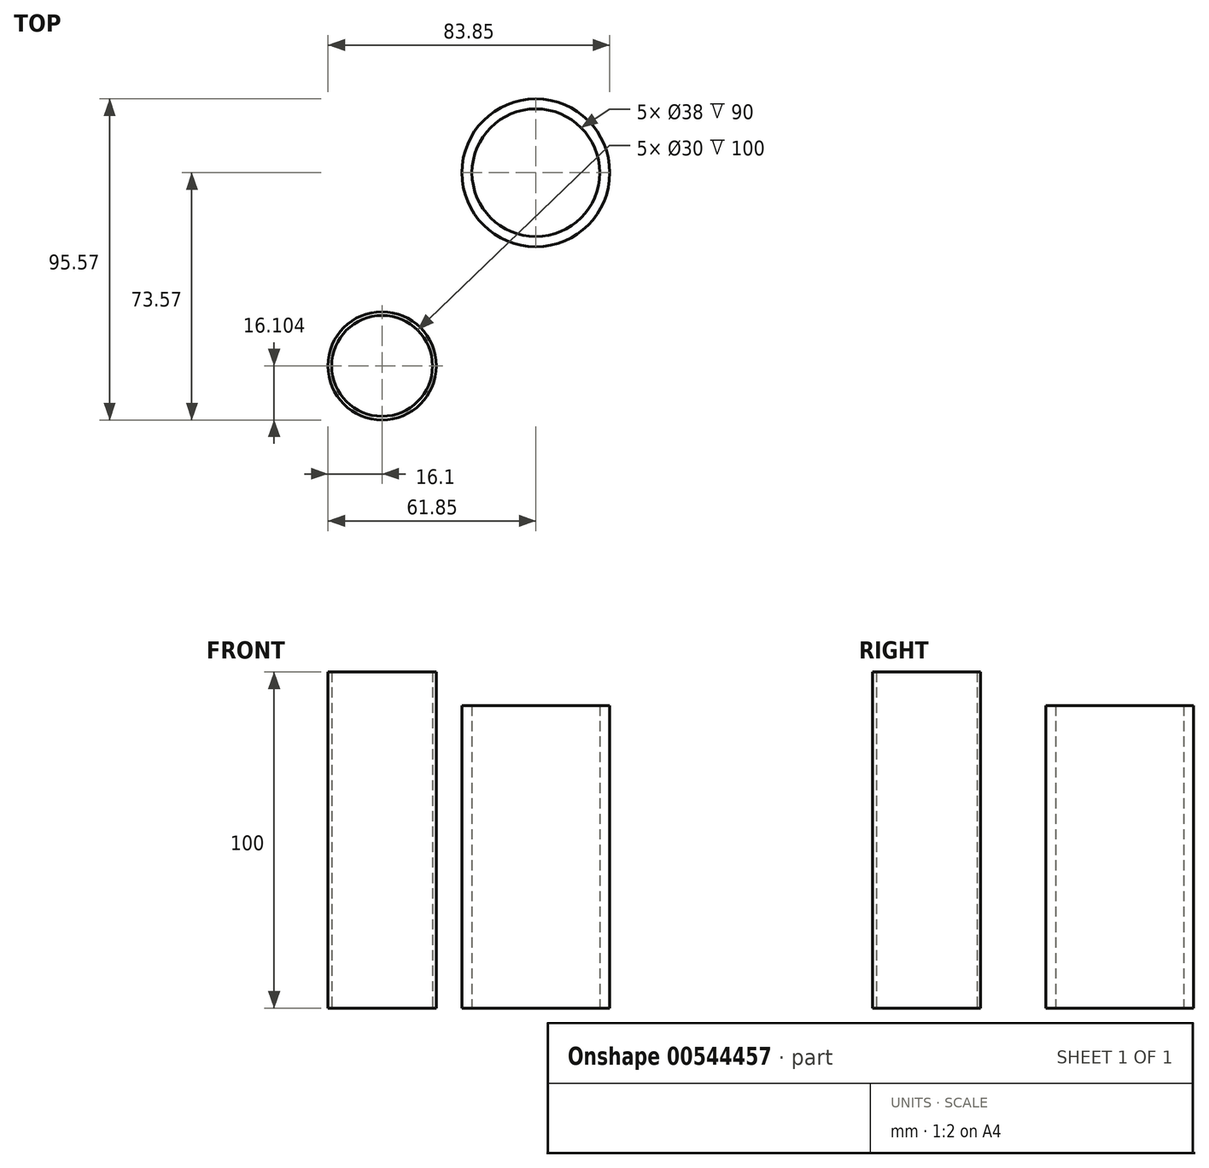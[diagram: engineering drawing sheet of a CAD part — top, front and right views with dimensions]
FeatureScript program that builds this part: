
annotation { "Feature Type Name" : "Feature", "Feature Type Description" : "" }
export const myFeature = defineFeature(function(context is Context, id is Id, definition is map)
    precondition{}
    {
        {
            var Q0;
            Q0=qCreatedBy(makeId("Top.planeOp"),FACE);
            var sketch = newSketch(context, id + "F0", { "sketchPlane" : qUnion([Q0])});
            skCircle(sketch, "E0", {"center": v(0, 0) * mm, "radius": 22 * mm});
            skCircle(sketch, "E1", {"center": v(0, 0) * mm, "radius": 19 * mm});
            skSolve(sketch);
        }
        {
            var Q0;
            Q0 = qSketchRegion(id + "F0", true);
            extrude(context, id + "F1", {"entities" : qUnion([Q0]), "depth" : 90 * mm, "offsetDistance" : 25 * mm});
        }
        {
            var Q0;
            Q0=qCreatedBy(makeId("Top.planeOp"),FACE);
            var sketch = newSketch(context, id + "F2", { "sketchPlane" : qUnion([Q0])});
            skCircle(sketch, "E2", {"center": v(-45.75, -57.47) * mm, "radius": 16.1 * mm});
            skCircle(sketch, "E3", {"center": v(-45.75, -57.47) * mm, "radius": 15 * mm});
            skSolve(sketch);
        }
        {
            var Q0;
            Q0=makeQuery(id+"F2.imprint","IMPRINT",FACE,{"disambiguationData":[TD([[makeQuery(id+"F2.imprint","IMPRINT",EDGE,{"derivedFrom":sQuery(id+"F2.wireOp",EDGE,"E2")}),1.0]])]});
            extrude(context, id + "F3", {"entities" : qUnion([Q0]), "depth" : 100 * mm, "offsetDistance" : 25 * mm});
        }
    });
